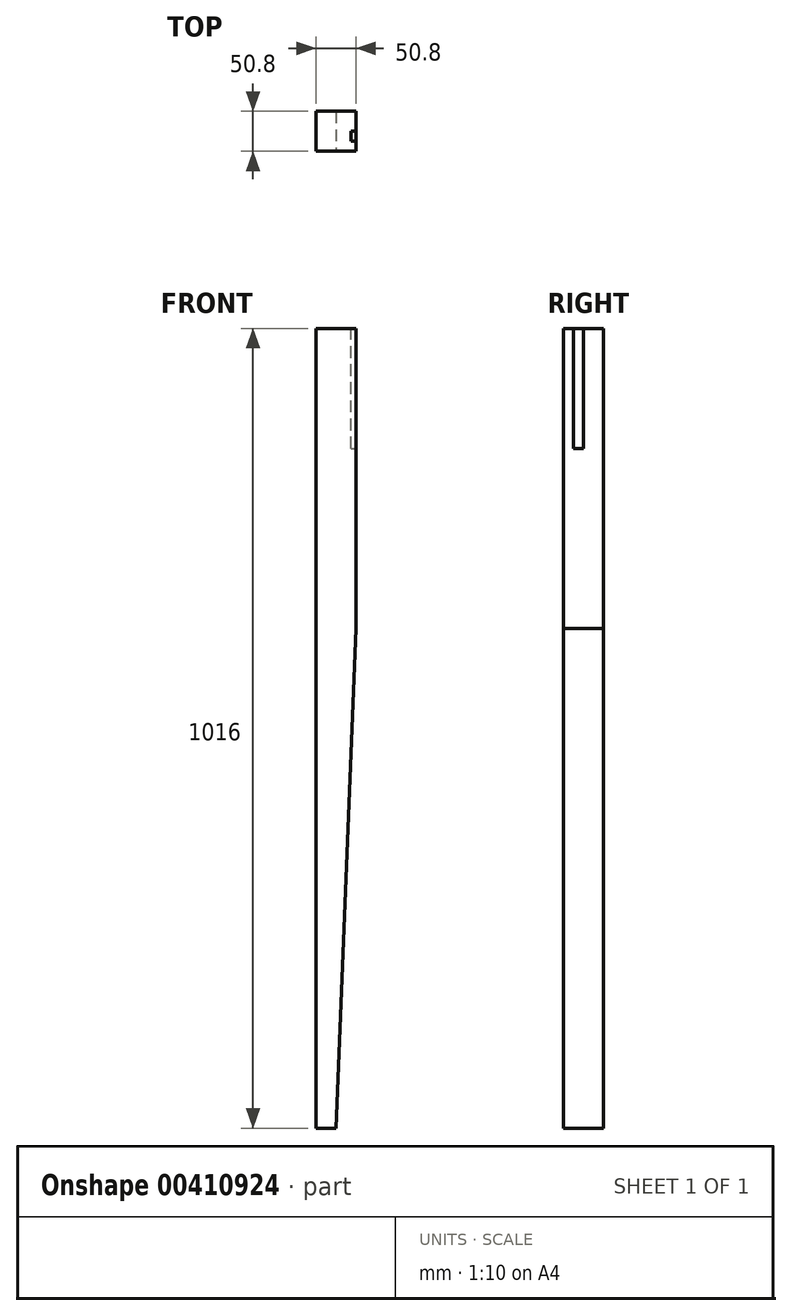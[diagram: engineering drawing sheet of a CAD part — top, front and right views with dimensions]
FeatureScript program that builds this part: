
annotation { "Feature Type Name" : "Feature", "Feature Type Description" : "" }
export const myFeature = defineFeature(function(context is Context, id is Id, definition is map)
    precondition{}
    {
        {
            var Q0;
            Q0=qCreatedBy(makeId("Front.planeOp"),FACE);
            var sketch = newSketch(context, id + "F0", { "sketchPlane" : qUnion([Q0])});
            skLineSegment(sketch, "E0", {"start": v(0, 0) * mm, "end": v(0, -1016) * mm});
            skLineSegment(sketch, "E1", {"start": v(0, -1016) * mm, "end": v(25.4, -1016) * mm});
            skLineSegment(sketch, "E2", {"start": v(25.4, -1016) * mm, "end": v(50.8, -381) * mm});
            skLineSegment(sketch, "E3", {"start": v(50.8, -381) * mm, "end": v(50.8, 0) * mm});
            skLineSegment(sketch, "E4", {"start": v(50.8, 0) * mm, "end": v(0, 0) * mm});
            skSolve(sketch);
        }
        {
            var Q0;
            Q0 = qSketchRegion(id + "F0", true);
            var Q1;
            Q1 = qSketchRegion(id + "FjrSAVhivZbbiHZ_1", true);
            extrude(context, id + "F1", {"entities" : qUnion([Q0, Q1]), "oppositeDirection" : true, "depth" : 50.8 * mm});
        }
        {
            var Q0;
            Q0=makeQuery(id+"F1.opExtrude","SWEPT_FACE",FACE,{"disambiguationData":[OSD([sQuery(id+"F0.wireOp",EDGE,"E3")])]});
            var sketch = newSketch(context, id + "F2", { "sketchPlane" : qUnion([Q0])});
            skLineSegment(sketch, "E5.bottom", {"start": v(25.4, -152.4) * mm, "end": v(12.7, -152.4) * mm});
            skLineSegment(sketch, "E5.top", {"start": v(25.4, 0) * mm, "end": v(12.7, 0) * mm});
            skLineSegment(sketch, "E5.left", {"start": v(25.4, -152.4) * mm, "end": v(25.4, 0) * mm});
            skLineSegment(sketch, "E5.right", {"start": v(12.7, -152.4) * mm, "end": v(12.7, 0) * mm});
            skSolve(sketch);
        }
        {
            var Q0;
            Q0 = qSketchRegion(id + "F2", true);
            extrude(context, id + "F3", {"entities" : qUnion([Q0]), "operationType" : NewBodyOperationType.REMOVE, "oppositeDirection" : true, "depth" : 6.35 * mm});
        }
    });
